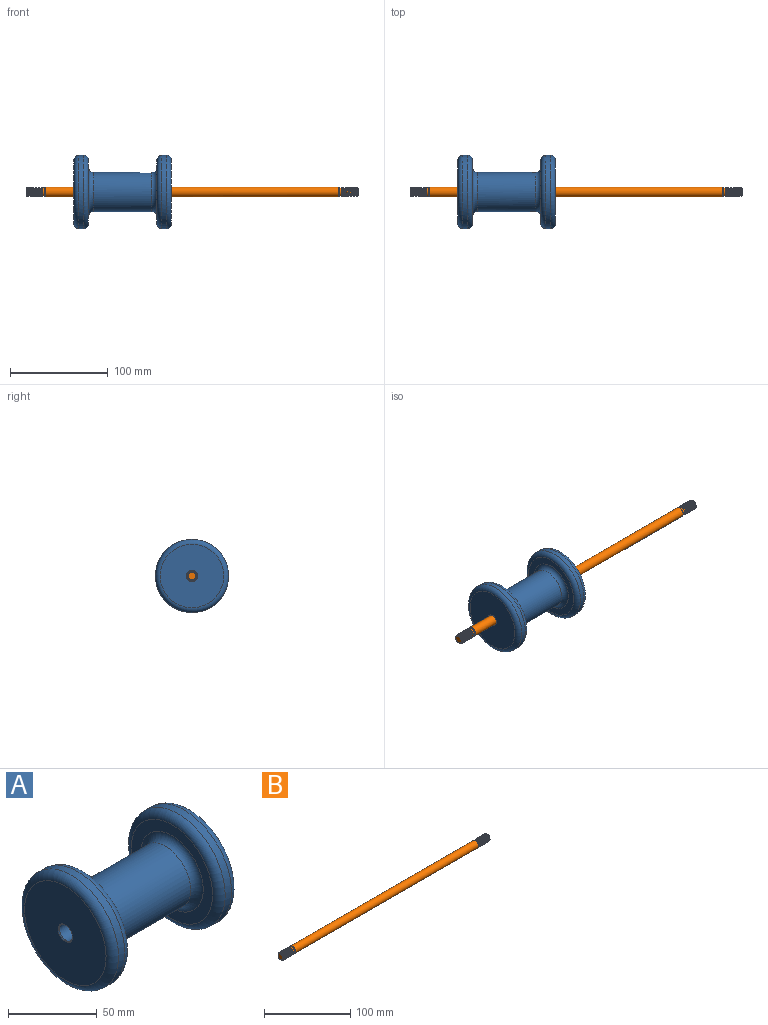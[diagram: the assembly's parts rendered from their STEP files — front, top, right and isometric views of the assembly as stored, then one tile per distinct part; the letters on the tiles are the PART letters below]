
ASSEMBLY  parts=2 mates=1
PART A: 16 faces, bbox 100x81.2x81.2 mm
  f0: plane 65x65mm, normal (-1,0,0), area 3214.4mm2, adj f13,f14
  f1: cylinder r=5.25mm len=99mm, axis (1,0,0), area 3265.7mm2, adj f14,f15
  f2: plane 65x65mm, normal (1,0,0), area 3214.4mm2, adj f8,f15
  f3: cylinder r=37.5mm len=75mm, axis (1,0,0), area 1178.1mm2, adj f8,f9
  f4: plane 65x65mm, normal (-1,0,0), area 1354.8mm2, adj f9,f10
  f5: cylinder r=20mm len=60mm, axis (1,0,0), area 7539.8mm2, adj f10,f11
  f6: plane 65x65mm, normal (1,0,0), area 1354.8mm2, adj f11,f12
  f7: cylinder r=37.5mm len=75mm, axis (1,0,0), area 1178.1mm2, adj f12,f13
  f8: torus R=32.5mm, axis (-1,0,0), area 1760.9mm2, adj f2,f3
  f9: torus R=32.5mm, axis (1,0,0), area 1760.9mm2, adj f3,f4
  f10: torus R=25mm, axis (1,0,0), area 1076.6mm2, adj f4,f5
  f11: torus R=25mm, axis (-1,0,0), area 1076.6mm2, adj f5,f6
  f12: torus R=32.5mm, axis (-1,0,0), area 1760.9mm2, adj f6,f7
  f13: torus R=32.5mm, axis (1,0,0), area 1760.9mm2, adj f0,f7
  f14: cone r=5.75mm half-angle=45deg, axis (-1,0,0), area 24.4mm2, adj f0,f1
  f15: cone r=5.25mm half-angle=45deg, axis (1,0,0), area 24.4mm2, adj f1,f2
PART B: 20 faces, bbox 341.8x11.6x11.6 mm
  f0: cylinder r=5mm len=15.15mm, axis (-1,0,0), area -22.6mm2, adj f9,f10,f16,f17,f19
  f1: cone r=4.15mm half-angle=30deg, axis (1,0,0), area 30mm2, adj f5,f6,f13,f14
  f2: cylinder r=4.15mm len=8.3mm, axis (-1,0,0), area 61.5mm2, adj f10,f12
  f3: plane 8x8mm, normal (-1,0,0), area 50.3mm2, adj f9,f18
  f4: plane 8.1x7.84mm, normal (1,0,0), area 49.5mm2, adj f8,f14,f15
  f5: cylinder r=5mm len=14.53mm, axis (-1,0,0), area 7mm2, adj f1,f8,f13,f14,f15
  f6: cylinder r=4.15mm len=8.3mm, axis (-1,0,0), area 52.2mm2, adj f1,f11
  f7: cylinder r=5mm len=300.3mm, axis (-1,0,0), area 9434.2mm2, adj f11,f12
  f8: cone r=5mm half-angle=45deg, axis (-1,0,0), area 15.1mm2, adj f4,f5,f14,f15
  f9: cone r=4mm half-angle=45deg, axis (1,0,0), area 15.1mm2, adj f0,f3,f17,f19
  f10: cone r=5mm half-angle=60deg, axis (-1,0,0), area 21mm2, adj f0,f2,f16,f19
  f11: cone r=5mm half-angle=45deg, axis (-1,0,0), area 34.6mm2, adj f6,f7
  f12: cone r=4.15mm half-angle=45deg, axis (1,0,0), area 34.6mm2, adj f2,f7
  f13: plane 1.12x1.12mm, normal (0,0.87,-0.5), area 0.5mm2, adj f1,f5,f14,f15
  f14: bspline ~17.25x11.55mm, area 429.4mm2, adj f1,f4,f5,f8,f13,f15
  f15: bspline ~17.25x11.55mm, area 420.7mm2, adj f4,f5,f8,f13,f14
  f16: plane 1.07x1mm, normal (0,1,0), area 0.6mm2, adj f0,f10,f17,f18,f19
  f17: bspline ~16.83x11.55mm, area 333.1mm2, adj f0,f9,f16,f18
  f18: cylinder r=4mm len=16.42mm, axis (1,0,0), area 105.6mm2, adj f3,f16,f17,f19
  f19: bspline ~17.08x11.55mm, area 346.7mm2, adj f0,f9,f10,f16,f18
PLACE A t=(24.53,-28.93,64.36)mm
PLACE B t=(-50.53,-28.93,64.36)mm fixed
MATE slider A.f1 <-> B.f0  axis (1,0,0) through (48.44,-28.93,64.36)mm
